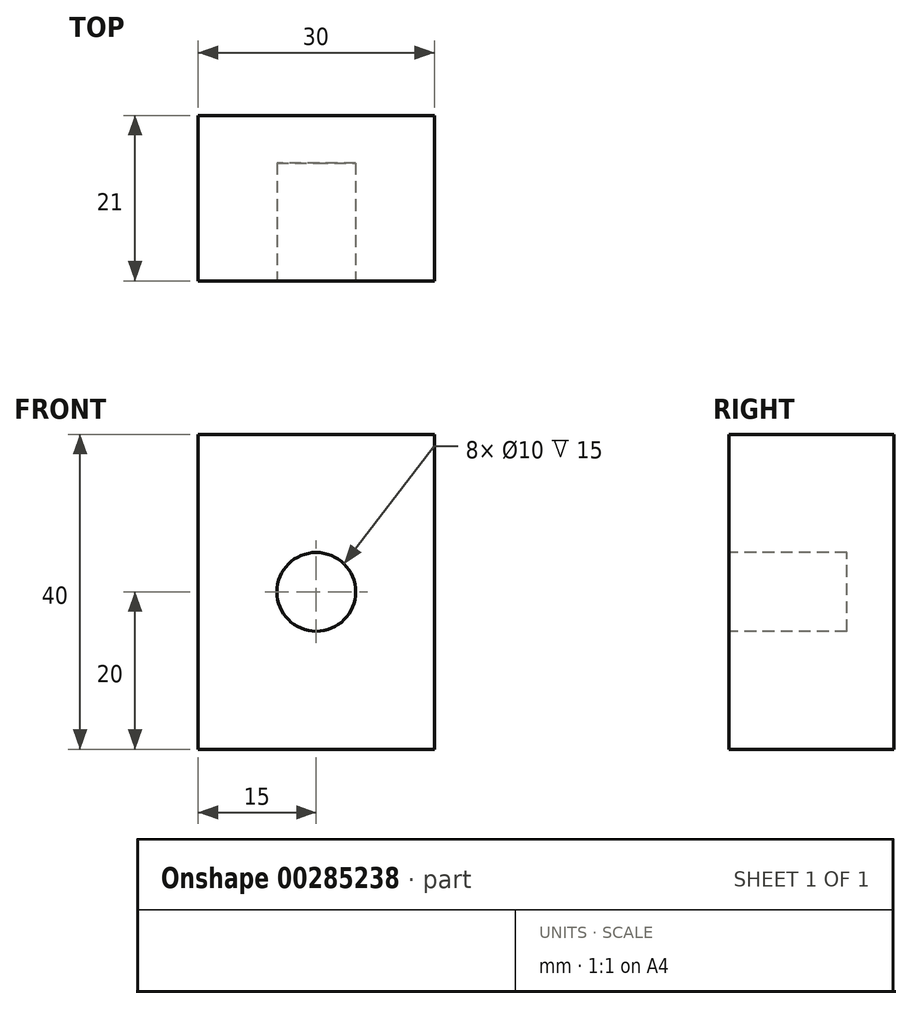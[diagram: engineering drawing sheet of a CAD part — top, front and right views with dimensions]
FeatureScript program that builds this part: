
annotation { "Feature Type Name" : "Feature", "Feature Type Description" : "" }
export const myFeature = defineFeature(function(context is Context, id is Id, definition is map)
    precondition{}
    {
        {
            var Q0;
            Q0=qCreatedBy(makeId("Front.planeOp"),FACE);
            var sketch = newSketch(context, id + "F0", { "sketchPlane" : qUnion([Q0])});
            skLineSegment(sketch, "E0.bottom", {"start": v(0, 0) * mm, "end": v(30, 0) * mm});
            skLineSegment(sketch, "E0.top", {"start": v(0, 40) * mm, "end": v(30, 40) * mm});
            skLineSegment(sketch, "E0.left", {"start": v(0, 0) * mm, "end": v(0, 40) * mm});
            skLineSegment(sketch, "E0.right", {"start": v(30, 0) * mm, "end": v(30, 40) * mm});
            skSolve(sketch);
        }
        {
            var Q0;
            Q0 = qSketchRegion(id + "F0", true);
            extrude(context, id + "F1", {"entities" : qUnion([Q0]), "depth" : 21 * mm});
        }
        {
            var Q0;
            Q0=makeQuery(id+"F1.opExtrude","CAP_FACE",FACE,{"disambiguationData":[OSD([sQuery(id+"F0.wireOp",EDGE,"E0.bottom"),sQuery(id+"F0.wireOp",EDGE,"E0.top"),sQuery(id+"F0.wireOp",EDGE,"E0.left"),sQuery(id+"F0.wireOp",EDGE,"E0.right")])],"isStart":false});
            var sketch = newSketch(context, id + "F2", { "sketchPlane" : qUnion([Q0])});
            skCircle(sketch, "E1", {"center": v(15, 20) * mm, "radius": 5 * mm});
            skPoint(sketch, "E1.centerSnap0", {"position": v(30, 20) * mm});
            skPoint(sketch, "E1.centerSnap1", {"position": v(15, 40) * mm});
            skSolve(sketch);
        }
        {
            var Q0;
            Q0 = qSketchRegion(id + "F2", true);
            extrude(context, id + "F3", {"entities" : qUnion([Q0]), "operationType" : NewBodyOperationType.REMOVE, "oppositeDirection" : true, "depth" : 15 * mm});
        }
    });
